# Revit family: 4401_Analog Photoelectric Smoke Detector
name_source: partatom
category: Fire Alarm Devices
units: mm (PartAtom-declared; Revit-internal decimal feet)

## family parameters
Cut with Voids When Loaded = No
Host = Face
Maintain Annotation Orientation = No
OmniClass Number = 23.85.30.21
OmniClass Title = Environmental Detection/Registration
Part Type = Normal
Room Calculation Point = No
Round Connector Dimension = Use Diameter
Shared = No

## types (1)
- 4401_Analog Photoelectric Smoke Detector
    Ambient Humidity = Maximum 95 % RH (Non condensing)
    Ambient Temperature Operating = -10 to +50 °C
    Ambient Temperature Storage = -25 to +75 °C
    Bases = Bases : 3312W
    CPR = 0786-CPR-21175
    Clearance Area = Clearance Area
    Current Active External LED = 1.8 mA
    Current Active Internal LED = 1.3 mA
    Current Quiescent = 0.3 mA (plus 0.025 if green polling LED is used)
    Default Elevation = 1200 mm
    Description = Analog photoelectric smoke detector, type number 4401_White
/ 44xx can be plugged in the base. 
The base is intended for indoor use and in dry premises.
    H_Base (mm) = 6 mm  [stored 0.019685 ft]
    H_Detector (mm) = 34 mm
    H_Total (mm) = 40 mm  [stored 0.131234 ft]
    Ingress Protection Rating = IP41
    Manufacturer = Panasonic
    Max_Wire Size = 1.6 mm
    Min_Wire Size = 0.6 mm
    Model = 4401W
    Omniclass Code = 23.85.30.21.11.11.11
    Omniclass Description = Smoke Detectors
    Product Material = Polycarbonate_Panasonic_White
    Short Circuit Isolator = No
    Tested and Approved = EN54-7
    Type Comments = Analog photoelectric smoke detector, type number 4401_White
/ 44xx can be plugged in the base. 
The base is intended for indoor use and in dry premises.
    URL = https://www.panasonic-fire-security.com
    Uniclass 2015 Code = Pr_75_80_30_27
    Uniclass 2015 Description = Fire and smoke detector bases
    Uniformat 2010  Code = D7050
    Uniformat 2010 Description = Detection and Alarm
    Vds Approval = EN54-7-VdS 2344
-VdS 2504
    Version = RVT20
    Voltage Allowed = 12 – 30 V DC
    Voltage Normal = 24V DC
    Weight = 75g
    ø (mm) = 102 mm

note: [stored X ft] marks values corroborated as IEEE doubles in the binary element streams (Revit-internal decimal feet)

## geometry (parser evidence)
native form markers: Blend x89, Sweep x13
no freeform markers — native parametric forms only
